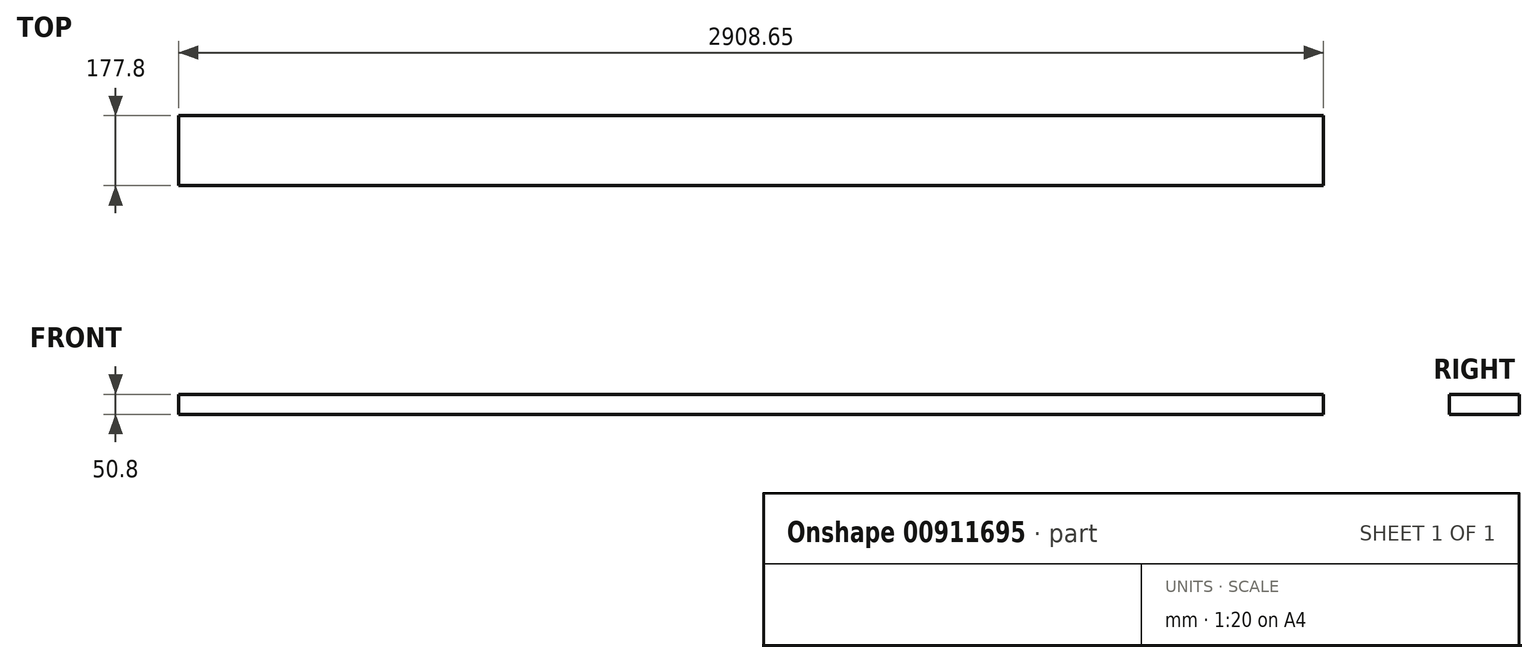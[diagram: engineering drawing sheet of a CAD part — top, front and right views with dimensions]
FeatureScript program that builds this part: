
annotation { "Feature Type Name" : "Feature", "Feature Type Description" : "" }
export const myFeature = defineFeature(function(context is Context, id is Id, definition is map)
    precondition{}
    {
        {
            var Q0;
            Q0=qCreatedBy(makeId("Top.planeOp"),FACE);
            var sketch = newSketch(context, id + "F0", { "sketchPlane" : qUnion([Q0])});
            skLineSegment(sketch, "E0.bottom", {"start": v(-308.69, -177.8) * mm, "end": v(2599.96, -177.8) * mm});
            skLineSegment(sketch, "E0.top", {"start": v(-308.69, 0) * mm, "end": v(2599.96, 0) * mm});
            skLineSegment(sketch, "E0.left", {"start": v(-308.69, -177.8) * mm, "end": v(-308.69, 0) * mm});
            skLineSegment(sketch, "E0.right", {"start": v(2599.96, -177.8) * mm, "end": v(2599.96, 0) * mm});
            skText(sketch, "E1", { "text": "12H", "fontName": "OpenSans-Bold.ttf"});
            const initialGuessF0  = {"E1": [-0.18169, 0, 1, 0, 1.016]};
            skSetInitialGuess(sketch, initialGuessF0);
            skSolve(sketch);
        }
        {
            var Q0;
            {var subQ0=sQuery(id+"F0.wireOp",EDGE,"d5d90416-0cdc-48ac-b64b-d5d0caaf983f.sketch_text.stroke-12");var subQ1=sQuery(id+"F0.wireOp",EDGE,"E0.top");var subQ2=makeQuery(id+"F0.imprint","INTERSECT",VERTEX,{"derivedFrom":[subQ1,subQ0]});Q0=makeQuery(id+"F0.imprint","IMPRINT",FACE,{"disambiguationData":[TD([[makeQuery(id+"F0.imprint","IMPRINT",EDGE,{"disambiguationData":[TD([[subQ2,-1.0]])],"derivedFrom":subQ1}),-1.0]])]});}
            var Q1;
            {var subQ6=sQuery(id+"F0.wireOp",EDGE,"d5d90416-0cdc-48ac-b64b-d5d0caaf983f.sketch_text.stroke-10");Q1=makeQuery(id+"F0.imprint","IMPRINT",FACE,{"disambiguationData":[TD([[makeQuery(id+"F0.imprint","IMPRINT",EDGE,{"derivedFrom":subQ6}),-1.0]])]});}
            var Q2;
            Q2=makeQuery(id+"F0.imprint","IMPRINT",FACE,{"disambiguationData":[TD([[makeQuery(id+"F0.imprint","IMPRINT",EDGE,{"derivedFrom":sQuery(id+"F0.wireOp",EDGE,"E0.bottom")}),1.0]])]});
            var Q3;
            Q3=makeQuery(id+"F0.imprint","IMPRINT",FACE,{"disambiguationData":[TD([[makeQuery(id+"F0.imprint","IMPRINT",EDGE,{"derivedFrom":sQuery(id+"F0.wireOp",EDGE,"d5d90416-0cdc-48ac-b64b-d5d0caaf983f.sketch_text.stroke-26")}),-1.0]])]});
            var Q4;
            Q4=makeQuery(id+"F0.imprint","IMPRINT",FACE,{"disambiguationData":[TD([[makeQuery(id+"F0.imprint","IMPRINT",EDGE,{"derivedFrom":sQuery(id+"F0.wireOp",EDGE,"d5d90416-0cdc-48ac-b64b-d5d0caaf983f.sketch_text.stroke-0")}),-1.0]])]});
            var Q5;
            Q5=makeQuery(id+"F0.imprint","IMPRINT",FACE,{"disambiguationData":[TD([[makeQuery(id+"F0.imprint","IMPRINT",EDGE,{"derivedFrom":sQuery(id+"F0.wireOp",EDGE,"eadfe806-04ac-4918-bb0a-3f37c2bbbc6a.sketch_text.stroke-10")}),-1.0]])]});
            var Q6;
            Q6=makeQuery(id+"F0.imprint","IMPRINT",FACE,{"disambiguationData":[TD([[makeQuery(id+"F0.imprint","IMPRINT",EDGE,{"derivedFrom":sQuery(id+"F0.wireOp",EDGE,"eadfe806-04ac-4918-bb0a-3f37c2bbbc6a.sketch_text.stroke-0")}),-1.0]])]});
            var Q7;
            Q7=makeQuery(id+"F0.imprint","IMPRINT",FACE,{"disambiguationData":[TD([[makeQuery(id+"F0.imprint","IMPRINT",EDGE,{"derivedFrom":sQuery(id+"F0.wireOp",EDGE,"eadfe806-04ac-4918-bb0a-3f37c2bbbc6a.sketch_text.stroke-20")}),-1.0]])]});
            var Q8;
            Q8=makeQuery(id+"F0.imprint","IMPRINT",FACE,{"disambiguationData":[TD([[makeQuery(id+"F0.imprint","IMPRINT",EDGE,{"derivedFrom":sQuery(id+"F0.wireOp",EDGE,"E1.sketch_text.stroke-0")}),-1.0]])]});
            var Q9;
            Q9=makeQuery(id+"F0.imprint","IMPRINT",FACE,{"disambiguationData":[TD([[makeQuery(id+"F0.imprint","IMPRINT",EDGE,{"derivedFrom":sQuery(id+"F0.wireOp",EDGE,"E1.sketch_text.stroke-10")}),-1.0]])]});
            var Q10;
            Q10=makeQuery(id+"F0.imprint","IMPRINT",FACE,{"disambiguationData":[TD([[makeQuery(id+"F0.imprint","IMPRINT",EDGE,{"derivedFrom":sQuery(id+"F0.wireOp",EDGE,"E1.sketch_text.stroke-34")}),-1.0]])]});
            extrude(context, id + "F1", {"entities" : qUnion([Q0, Q1, Q2, Q3, Q4, Q5, Q6, Q7, Q8, Q9, Q10]), "depth" : 50.8 * mm, "offsetDistance" : 25.4 * mm});
        }
    });
